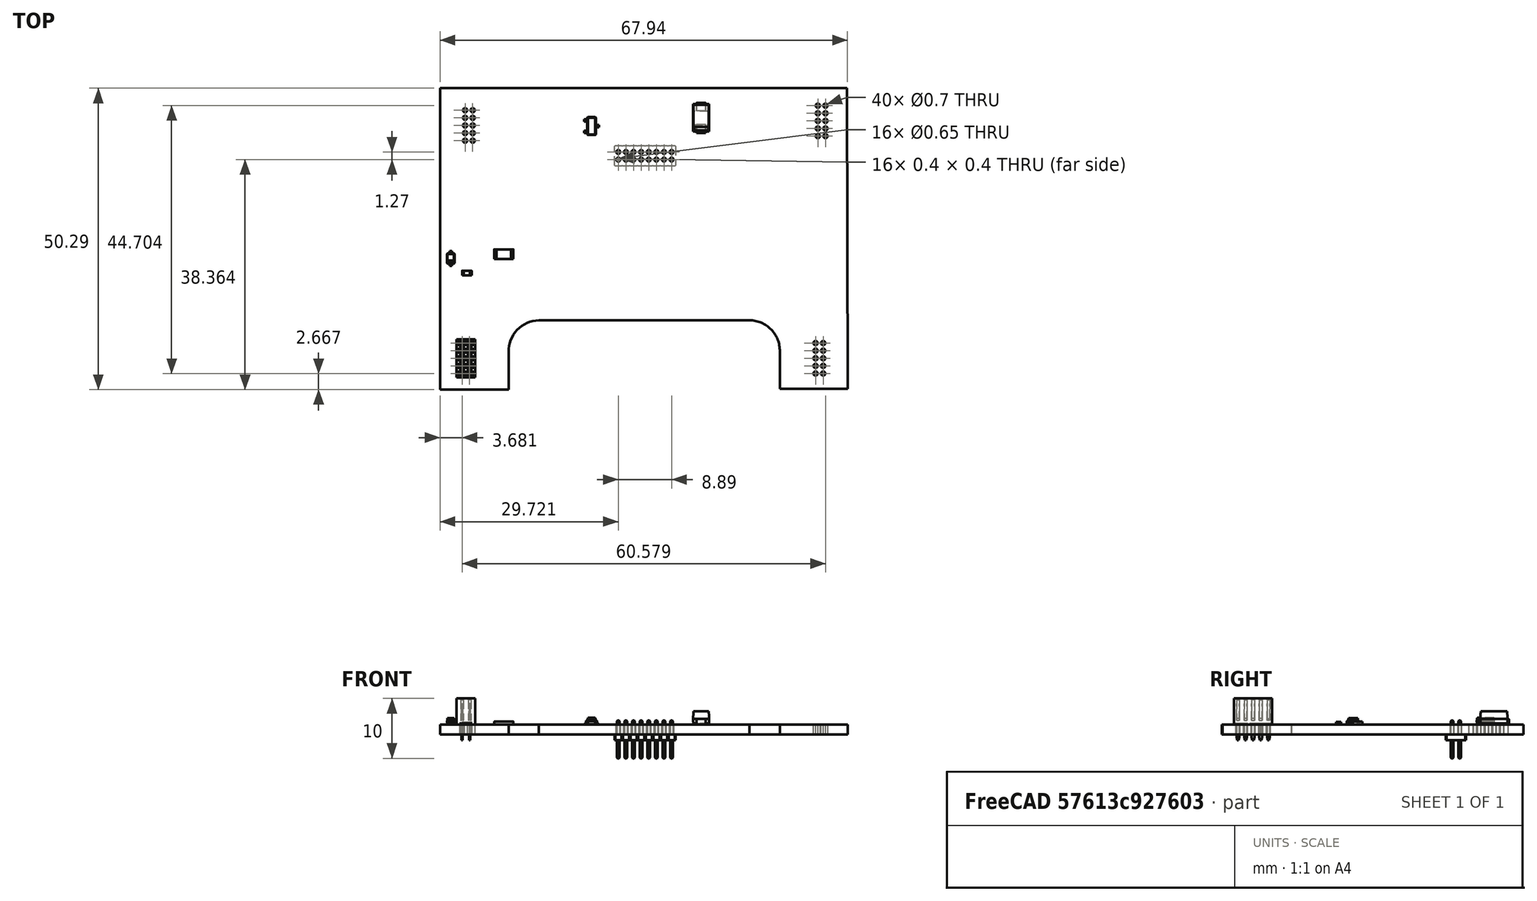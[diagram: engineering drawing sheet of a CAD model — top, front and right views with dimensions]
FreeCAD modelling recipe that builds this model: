
FCSTD DOCUMENT  (FreeCAD 1.0R39109 (Git))
Label: DIC_Addon
License: All rights reserved
LicenseURL: http://en.wikipedia.org/wiki/All_rights_reserved
objects: App::Link×70, Part::Feature×12, App::Part×5, PartDesign::CoordinateSystem×1, Sketcher::SketchObject×1
note: 15 computed .brp shape members not serialized (recipe doc carries the construction recipe); baked Part::Feature solids carry a one-line shape summary decoded from their .brp

FEATURE [PartDesign::CoordinateSystem] Local_CS_25db
  AttacherType = Attacher::AttachEngine3D
  MapMode = 2
FEATURE [Part::Feature] Pcb_25db
  shape: bbox 67.95 x 50.29 x 1.6 mm, 68 faces (baked)
FEATURE [Sketcher::SketchObject] PCB_Sketch_25db
  ArcFitTolerance = 1e-06
  FullyConstrained = false
  MakeInternals = false
  sketch-geometry (10):
    g0: LineSegment StartX=11.938 StartY=-11.938 StartZ=0 EndX=11.938 EndY=-62.23 EndZ=0
    g1: LineSegment StartX=68.58 StartY=-62.103 StartZ=0 EndX=79.883 EndY=-62.103 EndZ=0
    g2: LineSegment StartX=11.938 StartY=-62.23 StartZ=0 EndX=23.3806 EndY=-62.23 EndZ=0
    g3: LineSegment StartX=23.3806 StartY=-62.23 StartZ=0 EndX=23.368 EndY=-55.9897 EndZ=0
    g4: LineSegment StartX=79.756 StartY=-11.938 StartZ=0 EndX=11.938 EndY=-11.938 EndZ=0
    g5: LineSegment StartX=68.5926 StartY=-55.8627 StartZ=0 EndX=68.58 EndY=-62.103 EndZ=0
    g6: LineSegment StartX=28.448 StartY=-50.673 StartZ=0 EndX=63.5588 EndY=-50.6595 EndZ=0
    g7: LineSegment StartX=79.883 StartY=-62.103 StartZ=0 EndX=79.756 EndY=-11.938 EndZ=0
    g8: ArcOfCircle CenterX=28.5729 CenterY=-55.8776 CenterZ=0 NormalX=0 NormalY=0 NormalZ=-1 AngleXU=-0.0215457 Radius=5.20607 StartAngle=0 EndAngle=1.56835
    g9: ArcOfCircle CenterX=63.5 CenterY=-55.753 CenterZ=0 NormalX=0 NormalY=0 NormalZ=-1 AngleXU=1.58235 Radius=5.09379 StartAngle=-4.7832e-11 EndAngle=1.58079
  constraints (10):
    c: Coincident(g0,g2)
    c: Coincident(g0,g4)
    c: Coincident(g3,g8)
    c: Coincident(g2,g3)
    c: Coincident(g6,g8)
    c: Coincident(g6,g9)
    c: Coincident(g1,g5)
    c: Coincident(g5,g9)
    c: Coincident(g4,g7)
    c: Coincident(g1,g7)
FEATURE [Part::Feature] Shape  label="Q6_SOT_23_ffd5320711a5"
  Placement = pos=(37.211,-18.262,0) rot=(0,0,1;0rad)
  shape: bbox 2.5 x 3 x 1.2 mm, 76 faces (baked)
FEATURE [Part::Feature] Shape001  label="D16_D_SOD_323_d7651d96f6c3"
  Placement = pos=(13.7425,-40.366,0) rot=(0,0,1;1.5708rad)
  shape: bbox 1.25 x 2.5 x 1.1 mm, 67 faces (baked)
FEATURE [Part::Feature] Shape002  label="J6_PinSocket_2x05_P127mm_Vertical_83ee9fbb584e"
  Placement = pos=(16.891,-54.483,0) rot=(0,0,1;0rad)
  shape: bbox 3.05 x 6.35 x 7 mm, 320 faces (baked)
FEATURE [Part::Feature] Shape003  label="R41_R_0603_1608Metric_127fa2614279"
  Placement = pos=(16.433,-42.799,0) rot=(0,0,1;0rad)
  shape: bbox 1.6 x 0.8 x 0.45 mm, 26 faces (baked)
FEATURE [App::Link] R41_R_0603_1608Metric_127fa2614279_ln_  label="R12_R_0603_1608Metric_a0e0216bc4ce"
  LinkPlacement = pos=(30.861,-14.0945,0) rot=(0,0,1;1.5708rad)
  LinkedObject = -> Shape003
  Placement = pos=(30.861,-14.0945,0) rot=(0,0,1;1.5708rad)
FEATURE [App::Link] R41_R_0603_1608Metric_127fa2614279_ln_001  label="R13_R_0603_1608Metric_473b31106c1b"
  LinkPlacement = pos=(32.639,-18.77,0) rot=(0,0,1;1.5708rad)
  LinkedObject = -> Shape003
  Placement = pos=(32.639,-18.77,0) rot=(0,0,1;1.5708rad)
FEATURE [Part::Feature] Shape004  label="D6_D_SMA_735d77270f2b"
  Placement = pos=(55.477,-16.896,0) rot=(0,0,1;1.5708rad)
  shape: bbox 2.7 x 5 x 2.22 mm, 41 faces (baked)
FEATURE [App::Link] R41_R_0603_1608Metric_127fa2614279_ln_002  label="R9_R_0603_1608Metric_79f8a3dd54a6"
  LinkPlacement = pos=(61.214,-13.9059,0) rot=(0,0,1;3.14159rad)
  LinkedObject = -> Shape003
  Placement = pos=(61.214,-13.9059,0) rot=(0,0,1;3.14159rad)
FEATURE [App::Link] R41_R_0603_1608Metric_127fa2614279_ln_003  label="R31_R_0603_1608Metric_c49473b8d088"
  LinkPlacement = pos=(50.473,-46.8085,0) rot=(0,0,1;1.5708rad)
  LinkedObject = -> Shape003
  Placement = pos=(50.473,-46.8085,0) rot=(0,0,1;1.5708rad)
FEATURE [App::Link] R41_R_0603_1608Metric_127fa2614279_ln_004  label="R14_R_0603_1608Metric_d7197a96d642"
  LinkPlacement = pos=(37.41,-15.722,0) rot=(0,0,1;0rad)
  LinkedObject = -> Shape003
  Placement = pos=(37.41,-15.722,0) rot=(0,0,1;0rad)
FEATURE [App::Link] R41_R_0603_1608Metric_127fa2614279_ln_005  label="R35_R_0603_1608Metric_1226fcb64f1c"
  LinkPlacement = pos=(47.933,-37.9245,0) rot=(0,0,1;0rad)
  LinkedObject = -> Shape003
  Placement = pos=(47.933,-37.9245,0) rot=(0,0,1;0rad)
FEATURE [App::Link] D6_D_SMA_735d77270f2b_ln_  label="D17_D_SMA_0876cbf78d6f"
  LinkPlacement = pos=(20.828,-34.925,0) rot=(0,0,1;1.5708rad)
  LinkedObject = -> Shape004
  Placement = pos=(20.828,-34.925,0) rot=(0,0,1;1.5708rad)
FEATURE [App::Link] D6_D_SMA_735d77270f2b_ln_001  label="D15_D_SMA_1207fe425828"
  LinkPlacement = pos=(53.255,-43.21,0) rot=(0,0,1;0rad)
  LinkedObject = -> Shape004
  Placement = pos=(53.255,-43.21,0) rot=(0,0,1;0rad)
FEATURE [App::Link] D16_D_SOD_323_d7651d96f6c3_ln_  label="D13_D_SOD_323_07ad6b2cef4e"
  LinkPlacement = pos=(47.826,-32.3365,0) rot=(0,0,1;3.14159rad)
  LinkedObject = -> Shape001
  Placement = pos=(47.826,-32.3365,0) rot=(0,0,1;3.14159rad)
FEATURE [App::Link] R41_R_0603_1608Metric_127fa2614279_ln_006  label="R32_R_0603_1608Metric_48fbb2cf6ecc"
  LinkPlacement = pos=(56.061,-46.705,0) rot=(0,0,1;1.5708rad)
  LinkedObject = -> Shape003
  Placement = pos=(56.061,-46.705,0) rot=(0,0,1;1.5708rad)
FEATURE [App::Link] R41_R_0603_1608Metric_127fa2614279_ln_007  label="R24_R_0603_1608Metric_9565dda51c7b"
  LinkPlacement = pos=(50.461,-36.098,0) rot=(0,0,1;1.5708rad)
  LinkedObject = -> Shape003
  Placement = pos=(50.461,-36.098,0) rot=(0,0,1;1.5708rad)
FEATURE [App::Link] R41_R_0603_1608Metric_127fa2614279_ln_008  label="R39_R_0603_1608Metric_0d8059b3905e"
  LinkPlacement = pos=(27.857,-32.131,0) rot=(0,0,1;3.14159rad)
  LinkedObject = -> Shape003
  Placement = pos=(27.857,-32.131,0) rot=(0,0,1;3.14159rad)
FEATURE [App::Link] R41_R_0603_1608Metric_127fa2614279_ln_009  label="R11_R_0603_1608Metric_e8feb780e285"
  LinkPlacement = pos=(37.363,-14.198,0) rot=(0,0,1;0rad)
  LinkedObject = -> Shape003
  Placement = pos=(37.363,-14.198,0) rot=(0,0,1;0rad)
FEATURE [App::Link] D6_D_SMA_735d77270f2b_ln_002  label="D9_D_SMA_59bcf57c5f9f"
  LinkPlacement = pos=(51.943,-16.865,0) rot=(0,0,1;1.5708rad)
  LinkedObject = -> Shape004
  Placement = pos=(51.943,-16.865,0) rot=(0,0,1;1.5708rad)
FEATURE [App::Link] D6_D_SMA_735d77270f2b_ln_003  label="D18_D_SMA_56b2f2076145"
  LinkPlacement = pos=(24.362,-34.925,0) rot=(0,0,1;1.5708rad)
  LinkedObject = -> Shape004
  Placement = pos=(24.362,-34.925,0) rot=(0,0,1;1.5708rad)
FEATURE [App::Link] R41_R_0603_1608Metric_127fa2614279_ln_010  label="R37_R_0603_1608Metric_b9a5ae661070"
  LinkPlacement = pos=(17.25,-32.004,0) rot=(0,0,1;0rad)
  LinkedObject = -> Shape003
  Placement = pos=(17.25,-32.004,0) rot=(0,0,1;0rad)
FEATURE [App::Link] R41_R_0603_1608Metric_127fa2614279_ln_011  label="R34_R_0603_1608Metric_5b0c20e38f9c"
  LinkPlacement = pos=(44.504,-34.1145,0) rot=(0,0,1;3.14159rad)
  LinkedObject = -> Shape003
  Placement = pos=(44.504,-34.1145,0) rot=(0,0,1;3.14159rad)
FEATURE [App::Link] R41_R_0603_1608Metric_127fa2614279_ln_012  label="R33_R_0603_1608Metric_6760e7cc6251"
  LinkPlacement = pos=(44.0995,-32.3365,0) rot=(0,0,1;3.14159rad)
  LinkedObject = -> Shape003
  Placement = pos=(44.0995,-32.3365,0) rot=(0,0,1;3.14159rad)
FEATURE [App::Link] D16_D_SOD_323_d7651d96f6c3_ln_001  label="D4_D_SOD_323_fbe22daa305a"
  LinkPlacement = pos=(30.861,-18.2655,0) rot=(0,0,1;1.5708rad)
  LinkedObject = -> Shape001
  Placement = pos=(30.861,-18.2655,0) rot=(0,0,1;1.5708rad)
FEATURE [Part::Feature] Shape005  label="TH6_R_1206_3216Metric_a4174fc2a386"
  Placement = pos=(22.584,-39.624,0) rot=(0,0,1;3.14159rad)
  shape: bbox 3.2 x 1.6 x 0.55 mm, 26 faces (baked)
FEATURE [App::Link] R41_R_0603_1608Metric_127fa2614279_ln_013  label="R40_R_0603_1608Metric_99d0bb74b373"
  LinkPlacement = pos=(13.7425,-36.703,0) rot=(0,0,1;1.5708rad)
  LinkedObject = -> Shape003
  Placement = pos=(13.7425,-36.703,0) rot=(0,0,1;1.5708rad)
FEATURE [App::Link] R41_R_0603_1608Metric_127fa2614279_ln_014  label="R8_R_0603_1608Metric_f9849ceb0926"
  LinkPlacement = pos=(61.087,-19.4939,0) rot=(0,0,1;3.14159rad)
  LinkedObject = -> Shape003
  Placement = pos=(61.087,-19.4939,0) rot=(0,0,1;3.14159rad)
FEATURE [App::Link] R41_R_0603_1608Metric_127fa2614279_ln_015  label="R36_R_0603_1608Metric_b33a5e9c3cf1"
  LinkPlacement = pos=(17.377,-37.592,0) rot=(0,0,1;3.14159rad)
  LinkedObject = -> Shape003
  Placement = pos=(17.377,-37.592,0) rot=(0,0,1;3.14159rad)
FEATURE [App::Link] Q6_SOT_23_ffd5320711a5_ln_  label="Q18_SOT_23_5dae6c215293"
  LinkPlacement = pos=(16.6635,-40.259,0) rot=(0,0,1;3.14159rad)
  LinkedObject = -> Shape
  Placement = pos=(16.6635,-40.259,0) rot=(0,0,1;3.14159rad)
FEATURE [App::Link] J6_PinSocket_2x05_P127mm_Vertical_83ee9fbb584e_ln_  label="J2_PinSocket_2x05_P127mm_Vertical_fade8c78a2a7"
  LinkPlacement = pos=(76.2,-14.859,0) rot=(0,0,1;0rad)
  LinkedObject = -> Shape002
  Placement = pos=(76.2,-14.859,0) rot=(0,0,1;0rad)
FEATURE [App::Link] J6_PinSocket_2x05_P127mm_Vertical_83ee9fbb584e_ln_001  label="J5_PinSocket_2x05_P127mm_Vertical_c59673f5576a"
  LinkPlacement = pos=(16.129,-20.701,0) rot=(0,0,1;3.14159rad)
  LinkedObject = -> Shape002
  Placement = pos=(16.129,-20.701,0) rot=(0,0,1;3.14159rad)
FEATURE [App::Link] TH6_R_1206_3216Metric_a4174fc2a386_ln_  label="TH2_R_1206_3216Metric_52bc38417804"
  LinkPlacement = pos=(41.529,-18.262,0) rot=(0,0,1;1.5708rad)
  LinkedObject = -> Shape005
  Placement = pos=(41.529,-18.262,0) rot=(0,0,1;1.5708rad)
FEATURE [App::Link] D6_D_SMA_735d77270f2b_ln_004  label="D14_D_SMA_40db2f55f09c"
  LinkPlacement = pos=(53.255,-39.584,0) rot=(0,0,1;0rad)
  LinkedObject = -> Shape004
  Placement = pos=(53.255,-39.584,0) rot=(0,0,1;0rad)
FEATURE [App::Link] R41_R_0603_1608Metric_127fa2614279_ln_016  label="R42_R_0603_1608Metric_3962cb7ffa21"
  LinkPlacement = pos=(19.3305,-40.386,0) rot=(0,0,1;1.5708rad)
  LinkedObject = -> Shape003
  Placement = pos=(19.3305,-40.386,0) rot=(0,0,1;1.5708rad)
FEATURE [App::Link] J6_PinSocket_2x05_P127mm_Vertical_83ee9fbb584e_ln_002  label="J4_PinSocket_2x05_P127mm_Vertical_839abc38b667"
  LinkPlacement = pos=(75.819,-54.473,0) rot=(0,0,1;0rad)
  LinkedObject = -> Shape002
  Placement = pos=(75.819,-54.473,0) rot=(0,0,1;0rad)
FEATURE [App::Link] R41_R_0603_1608Metric_127fa2614279_ln_017  label="R10_R_0603_1608Metric_f7e09fcf0586"
  LinkPlacement = pos=(48.387,-13.563,0) rot=(0,0,1;3.14159rad)
  LinkedObject = -> Shape003
  Placement = pos=(48.387,-13.563,0) rot=(0,0,1;3.14159rad)
FEATURE [App::Link] R41_R_0603_1608Metric_127fa2614279_ln_018  label="R38_R_0603_1608Metric_5053fa264887"
  LinkPlacement = pos=(27.984,-37.719,0) rot=(0,0,1;3.14159rad)
  LinkedObject = -> Shape003
  Placement = pos=(27.984,-37.719,0) rot=(0,0,1;3.14159rad)
FEATURE [App::Link] R41_R_0603_1608Metric_127fa2614279_ln_019  label="R30_R_0603_1608Metric_0ef8a02bf31b"
  LinkPlacement = pos=(56.061,-36.0085,0) rot=(0,0,-1;1.5708rad)
  LinkedObject = -> Shape003
  Placement = pos=(56.061,-36.0085,0) rot=(0,0,-1;1.5708rad)
FEATURE [App::Link] Q6_SOT_23_ffd5320711a5_ln_001  label="Q15_SOT_23_f88ca606a138"
  LinkPlacement = pos=(47.933,-35.2575,0) rot=(0,0,1;1.5708rad)
  LinkedObject = -> Shape
  Placement = pos=(47.933,-35.2575,0) rot=(0,0,1;1.5708rad)
FEATURE [App::Link] TH6_R_1206_3216Metric_a4174fc2a386_ln_001  label="TH4_R_1206_3216Metric_6cedd577e318"
  LinkPlacement = pos=(48.568,-41.178,0) rot=(0,0,1;1.5708rad)
  LinkedObject = -> Shape005
  Placement = pos=(48.568,-41.178,0) rot=(0,0,1;1.5708rad)
FEATURE [App::Link] R41_R_0603_1608Metric_127fa2614279_ln_020  label="R5_R_0603_1608Metric_a69d22cc4bcb"
  LinkPlacement = pos=(38.6475,-31.119,0) rot=(0,0,-1;1.5708rad)
  LinkedObject = -> Shape003
  Placement = pos=(38.6475,-31.119,0) rot=(0,0,-1;1.5708rad)
FEATURE [App::Part] Top_25db
  Group = -> [Shape,Shape001,Shape002,Shape003,R41_R_0603_1608Metric_127fa2614279_ln_,R41_R_0603_1608Metric_127fa2614279_ln_001,Shape004,R41_R_0603_1608Metric_127fa2614279_ln_002,R41_R_0603_1608Metric_127fa2614279_ln_003,R41_R_0603_1608Metric_127fa2614279_ln_004,R41_R_0603_1608Metric_127fa2614279_ln_005,D6_D_SMA_735d77270f2b_ln_,D6_D_SMA_735d77270f2b_ln_001,D16_D_SOD_323_d7651d96f6c3_ln_,+27 more]
  Origin = -> Origin003
FEATURE [App::Link] R41_R_0603_1608Metric_127fa2614279_ln_021  label="R16_R_0603_1608Metric_7932c1e08af1"
  LinkPlacement = pos=(41.275,-42.313,-1.6) rot=(0.707107,0.707107,0;3.14159rad)
  LinkedObject = -> Shape003
  Placement = pos=(41.275,-42.313,-1.6) rot=(0.707107,0.707107,0;3.14159rad)
FEATURE [App::Link] R41_R_0603_1608Metric_127fa2614279_ln_022  label="R25_R_0603_1608Metric_af43064dc6b6"
  LinkPlacement = pos=(74.996,-34.8215,-1.6) rot=(0.707107,-0.707107,0;3.14159rad)
  LinkedObject = -> Shape003
  Placement = pos=(74.996,-34.8215,-1.6) rot=(0.707107,-0.707107,0;3.14159rad)
FEATURE [App::Link] R41_R_0603_1608Metric_127fa2614279_ln_023  label="R3_R_0603_1608Metric_90eb9fac611c"
  LinkPlacement = pos=(27.8525,-37.777,-1.6) rot=(0.707107,0.707107,0;3.14159rad)
  LinkedObject = -> Shape003
  Placement = pos=(27.8525,-37.777,-1.6) rot=(0.707107,0.707107,0;3.14159rad)
FEATURE [App::Link] R41_R_0603_1608Metric_127fa2614279_ln_024  label="R2_R_0603_1608Metric_a95339afed33"
  LinkPlacement = pos=(22.3534,-27.095,-1.6) rot=(0.707107,0.707107,0;3.14159rad)
  LinkedObject = -> Shape003
  Placement = pos=(22.3534,-27.095,-1.6) rot=(0.707107,0.707107,0;3.14159rad)
FEATURE [App::Link] R41_R_0603_1608Metric_127fa2614279_ln_025  label="R29_R_0603_1608Metric_a323e5d2541c"
  LinkPlacement = pos=(69.088,-31.2255,-1.6) rot=(0.707107,-0.707107,0;3.14159rad)
  LinkedObject = -> Shape003
  Placement = pos=(69.088,-31.2255,-1.6) rot=(0.707107,-0.707107,0;3.14159rad)
FEATURE [App::Link] R41_R_0603_1608Metric_127fa2614279_ln_026  label="R1_R_0603_1608Metric_b07fb1c3085f"
  LinkPlacement = pos=(27.9414,-27.222,-1.6) rot=(0.707107,0.707107,0;3.14159rad)
  LinkedObject = -> Shape003
  Placement = pos=(27.9414,-27.222,-1.6) rot=(0.707107,0.707107,0;3.14159rad)
FEATURE [App::Link] R41_R_0603_1608Metric_127fa2614279_ln_027  label="R18_R_0603_1608Metric_5d82281689e8"
  LinkPlacement = pos=(26.7885,-42.672,-1.6) rot=(0,1,0;3.14159rad)
  LinkedObject = -> Shape003
  Placement = pos=(26.7885,-42.672,-1.6) rot=(0,1,0;3.14159rad)
FEATURE [App::Link] R41_R_0603_1608Metric_127fa2614279_ln_028  label="R27_R_0603_1608Metric_214af474eae8"
  LinkPlacement = pos=(75.9085,-41.275,-1.6) rot=(1,0,0;3.14159rad)
  LinkedObject = -> Shape003
  Placement = pos=(75.9085,-41.275,-1.6) rot=(1,0,0;3.14159rad)
FEATURE [App::Link] D6_D_SMA_735d77270f2b_ln_005  label="D11_D_SMA_1ba17688d2f4"
  LinkPlacement = pos=(38.449,-38.735,-1.6) rot=(1,0,0;3.14159rad)
  LinkedObject = -> Shape004
  Placement = pos=(38.449,-38.735,-1.6) rot=(1,0,0;3.14159rad)
FEATURE [App::Link] R41_R_0603_1608Metric_127fa2614279_ln_029  label="R17_R_0603_1608Metric_89ce4ec7833c"
  LinkPlacement = pos=(26.8355,-48.26,-1.6) rot=(1,0,0;3.14159rad)
  LinkedObject = -> Shape003
  Placement = pos=(26.8355,-48.26,-1.6) rot=(1,0,0;3.14159rad)
FEATURE [App::Link] R41_R_0603_1608Metric_127fa2614279_ln_030  label="R6_R_0603_1608Metric_1afd86b5277d"
  LinkPlacement = pos=(35.7265,-28.421,-1.6) rot=(0.707107,0.707107,0;3.14159rad)
  LinkedObject = -> Shape003
  Placement = pos=(35.7265,-28.421,-1.6) rot=(0.707107,0.707107,0;3.14159rad)
FEATURE [App::Link] D16_D_SOD_323_d7651d96f6c3_ln_002  label="D10_D_SOD_323_00e277693b72"
  LinkPlacement = pos=(33.167,-46.0745,-1.6) rot=(0,1,0;3.14159rad)
  LinkedObject = -> Shape001
  Placement = pos=(33.167,-46.0745,-1.6) rot=(0,1,0;3.14159rad)
FEATURE [Part::Feature] Shape006  label="J3_PinHeader_2x08_P127mm_Vertical_13ff719d442c"
  Placement = pos=(50.551,-23.866,-1.6) rot=(0.707107,0.707107,0;3.14159rad)
  shape: bbox 10.16 x 3.4 x 6.3 mm, 340 faces (baked)
FEATURE [App::Link] D6_D_SMA_735d77270f2b_ln_006  label="D3_D_SMA_cd35c1e422c8"
  LinkPlacement = pos=(25.0905,-34.268,-1.6) rot=(0,1,0;3.14159rad)
  LinkedObject = -> Shape004
  Placement = pos=(25.0905,-34.268,-1.6) rot=(0,1,0;3.14159rad)
FEATURE [App::Link] R41_R_0603_1608Metric_127fa2614279_ln_031  label="R7_R_0603_1608Metric_afc0888e760f"
  LinkPlacement = pos=(30.6465,-28.172,-1.6) rot=(0.707107,-0.707107,0;3.14159rad)
  LinkedObject = -> Shape003
  Placement = pos=(30.6465,-28.172,-1.6) rot=(0.707107,-0.707107,0;3.14159rad)
FEATURE [App::Link] R41_R_0603_1608Metric_127fa2614279_ln_032  label="R28_R_0603_1608Metric_a4707fec901c"
  LinkPlacement = pos=(61.595,-31.0515,-1.6) rot=(0.707107,0.707107,0;3.14159rad)
  LinkedObject = -> Shape003
  Placement = pos=(61.595,-31.0515,-1.6) rot=(0.707107,0.707107,0;3.14159rad)
FEATURE [App::Link] D16_D_SOD_323_d7651d96f6c3_ln_003  label="D5_D_SOD_323_8140ef0d37c0"
  LinkPlacement = pos=(63.373,-31.095,-1.6) rot=(0.707107,0.707107,0;3.14159rad)
  LinkedObject = -> Shape001
  Placement = pos=(63.373,-31.095,-1.6) rot=(0.707107,0.707107,0;3.14159rad)
FEATURE [App::Link] D16_D_SOD_323_d7651d96f6c3_ln_004  label="D1_D_SOD_323_d5d77308ac17"
  LinkPlacement = pos=(33.1665,-31.347,-1.6) rot=(1,0,0;3.14159rad)
  LinkedObject = -> Shape001
  Placement = pos=(33.1665,-31.347,-1.6) rot=(1,0,0;3.14159rad)
FEATURE [App::Link] Q6_SOT_23_ffd5320711a5_ln_002  label="Q10_SOT_23_8cad5c28a702"
  LinkPlacement = pos=(33.147,-43.0265,-1.6) rot=(0.707107,-0.707107,0;3.14159rad)
  LinkedObject = -> Shape
  Placement = pos=(33.147,-43.0265,-1.6) rot=(0.707107,-0.707107,0;3.14159rad)
FEATURE [App::Link] R41_R_0603_1608Metric_127fa2614279_ln_033  label="R23_R_0603_1608Metric_7848ec0b3468"
  LinkPlacement = pos=(65.151,-41.529,-1.6) rot=(1,0,0;3.14159rad)
  LinkedObject = -> Shape003
  Placement = pos=(65.151,-41.529,-1.6) rot=(1,0,0;3.14159rad)
FEATURE [App::Link] TH6_R_1206_3216Metric_a4174fc2a386_ln_002  label="TH5_R_1206_3216Metric_65273da20f15"
  LinkPlacement = pos=(70.612,-34.036,-1.6) rot=(0,1,0;3.14159rad)
  LinkedObject = -> Shape005
  Placement = pos=(70.612,-34.036,-1.6) rot=(0,1,0;3.14159rad)
FEATURE [App::Link] R41_R_0603_1608Metric_127fa2614279_ln_034  label="R19_R_0603_1608Metric_b451ed5a0d5d"
  LinkPlacement = pos=(30.607,-40.6135,-1.6) rot=(0.707107,-0.707107,0;3.14159rad)
  LinkedObject = -> Shape003
  Placement = pos=(30.607,-40.6135,-1.6) rot=(0.707107,-0.707107,0;3.14159rad)
FEATURE [App::Link] R41_R_0603_1608Metric_127fa2614279_ln_035  label="R21_R_0603_1608Metric_086685fbb64e"
  LinkPlacement = pos=(64.262,-35.0285,-1.6) rot=(0.707107,0.707107,0;3.14159rad)
  LinkedObject = -> Shape003
  Placement = pos=(64.262,-35.0285,-1.6) rot=(0.707107,0.707107,0;3.14159rad)
FEATURE [App::Link] R41_R_0603_1608Metric_127fa2614279_ln_036  label="R20_R_0603_1608Metric_74876393d18b"
  LinkPlacement = pos=(37.211,-46.0745,-1.6) rot=(1,0,0;3.14159rad)
  LinkedObject = -> Shape003
  Placement = pos=(37.211,-46.0745,-1.6) rot=(1,0,0;3.14159rad)
FEATURE [App::Link] R41_R_0603_1608Metric_127fa2614279_ln_037  label="R15_R_0603_1608Metric_62f7b17bc8fc"
  LinkPlacement = pos=(35.687,-42.313,-1.6) rot=(0.707107,-0.707107,0;3.14159rad)
  LinkedObject = -> Shape003
  Placement = pos=(35.687,-42.313,-1.6) rot=(0.707107,-0.707107,0;3.14159rad)
FEATURE [App::Link] D6_D_SMA_735d77270f2b_ln_007  label="D2_D_SMA_e8f0f4ea1691"
  LinkPlacement = pos=(25.0905,-30.734,-1.6) rot=(0,1,0;3.14159rad)
  LinkedObject = -> Shape004
  Placement = pos=(25.0905,-30.734,-1.6) rot=(0,1,0;3.14159rad)
FEATURE [App::Link] TH6_R_1206_3216Metric_a4174fc2a386_ln_003  label="TH1_R_1206_3216Metric_ce9414de59a2"
  LinkPlacement = pos=(29.8845,-32.617,-1.6) rot=(0.707107,0.707107,0;3.14159rad)
  LinkedObject = -> Shape005
  Placement = pos=(29.8845,-32.617,-1.6) rot=(0.707107,0.707107,0;3.14159rad)
FEATURE [App::Link] D6_D_SMA_735d77270f2b_ln_008  label="D12_D_SMA_21d0ff51f2b2"
  LinkPlacement = pos=(38.449,-35.201,-1.6) rot=(1,0,0;3.14159rad)
  LinkedObject = -> Shape004
  Placement = pos=(38.449,-35.201,-1.6) rot=(1,0,0;3.14159rad)
FEATURE [App::Link] TH6_R_1206_3216Metric_a4174fc2a386_ln_004  label="TH3_R_1206_3216Metric_be97d367e00d"
  LinkPlacement = pos=(33.782,-36.852,-1.6) rot=(0.707107,-0.707107,0;3.14159rad)
  LinkedObject = -> Shape005
  Placement = pos=(33.782,-36.852,-1.6) rot=(0.707107,-0.707107,0;3.14159rad)
FEATURE [App::Link] D6_D_SMA_735d77270f2b_ln_009  label="D8_D_SMA_7218f854b2e2"
  LinkPlacement = pos=(72.39,-38.703,-1.6) rot=(0.707107,-0.707107,0;3.14159rad)
  LinkedObject = -> Shape004
  Placement = pos=(72.39,-38.703,-1.6) rot=(0.707107,-0.707107,0;3.14159rad)
FEATURE [App::Link] Q6_SOT_23_ffd5320711a5_ln_003  label="Q3_SOT_23_dc7f19c19d1b"
  LinkPlacement = pos=(33.1865,-28.299,-1.6) rot=(0.707107,-0.707107,0;3.14159rad)
  LinkedObject = -> Shape
  Placement = pos=(33.1865,-28.299,-1.6) rot=(0.707107,-0.707107,0;3.14159rad)
FEATURE [App::Link] R41_R_0603_1608Metric_127fa2614279_ln_038  label="R4_R_0603_1608Metric_2e89caf32d98"
  LinkPlacement = pos=(22.2645,-37.8005,-1.6) rot=(0.707107,-0.707107,0;3.14159rad)
  LinkedObject = -> Shape003
  Placement = pos=(22.2645,-37.8005,-1.6) rot=(0.707107,-0.707107,0;3.14159rad)
FEATURE [App::Link] R41_R_0603_1608Metric_127fa2614279_ln_039  label="R22_R_0603_1608Metric_94414fea2e43"
  LinkPlacement = pos=(33.1235,-40.3595,-1.6) rot=(1,0,0;3.14159rad)
  LinkedObject = -> Shape003
  Placement = pos=(33.1235,-40.3595,-1.6) rot=(1,0,0;3.14159rad)
FEATURE [App::Link] D6_D_SMA_735d77270f2b_ln_010  label="D7_D_SMA_2e44e889cb4e"
  LinkPlacement = pos=(68.834,-38.703,-1.6) rot=(0.707107,-0.707107,0;3.14159rad)
  LinkedObject = -> Shape004
  Placement = pos=(68.834,-38.703,-1.6) rot=(0.707107,-0.707107,0;3.14159rad)
FEATURE [App::Link] R41_R_0603_1608Metric_127fa2614279_ln_040  label="R26_R_0603_1608Metric_d41138b5fa4f"
  LinkPlacement = pos=(64.389,-28.281,-1.6) rot=(1,0,0;3.14159rad)
  LinkedObject = -> Shape003
  Placement = pos=(64.389,-28.281,-1.6) rot=(1,0,0;3.14159rad)
FEATURE [App::Link] Q6_SOT_23_ffd5320711a5_ln_004  label="Q12_SOT_23_6e3906f2bc9c"
  LinkPlacement = pos=(66.421,-31.202,-1.6) rot=(0,1,0;3.14159rad)
  LinkedObject = -> Shape
  Placement = pos=(66.421,-31.202,-1.6) rot=(0,1,0;3.14159rad)
FEATURE [App::Part] Bot_25db
  Group = -> [R41_R_0603_1608Metric_127fa2614279_ln_021,R41_R_0603_1608Metric_127fa2614279_ln_022,R41_R_0603_1608Metric_127fa2614279_ln_023,R41_R_0603_1608Metric_127fa2614279_ln_024,R41_R_0603_1608Metric_127fa2614279_ln_025,R41_R_0603_1608Metric_127fa2614279_ln_026,R41_R_0603_1608Metric_127fa2614279_ln_027,R41_R_0603_1608Metric_127fa2614279_ln_028,D6_D_SMA_735d77270f2b_ln_005,+27 more]
  Origin = -> Origin004
FEATURE [App::Part] Step_Models_25db
  Group = -> [Top_25db,Bot_25db]
  Origin = -> Origin002
FEATURE [Part::Feature] Shape008  label="topTracks_25db"
  Placement = pos=(0,0,0.01) rot=(0,0,1;0rad)
  shape: bbox 49.04 x 37.37 x 2e-07 mm, 64 faces, 0 solids (baked)
FEATURE [Part::Feature] topPads_25db_  label="topPads_25db_cut"
  Placement = pos=(0,0,0.02) rot=(0,0,1;0rad)
  shape: bbox 65.44 x 47.66 x 0.0001004 mm, 213 faces, 0 solids (baked)
FEATURE [Part::Feature] Shape010  label="botTracks_25db"
  Placement = pos=(0,0,-1.61) rot=(0,0,1;0rad)
  shape: bbox 55.06 x 15.48 x 2e-07 mm, 32 faces, 0 solids (baked)
FEATURE [Part::Feature] botPads_25db_  label="botPads_25db_cut"
  Placement = pos=(0,0,-1.62) rot=(0,0,1;0rad)
  shape: bbox 65.44 x 47.66 x 0.0001004 mm, 209 faces, 0 solids (baked)
FEATURE [App::Part] Board_Geoms_25db
  Group = -> [Pcb_25db,PCB_Sketch_25db,topPads_25db_,Shape008,botPads_25db_,Shape010]
  Origin = -> Origin
FEATURE [App::Part] Board_25db  label="DIC_Addon"
  Group = -> [Local_CS_25db,Board_Geoms_25db,Step_Models_25db]
  Origin = -> Origin001
